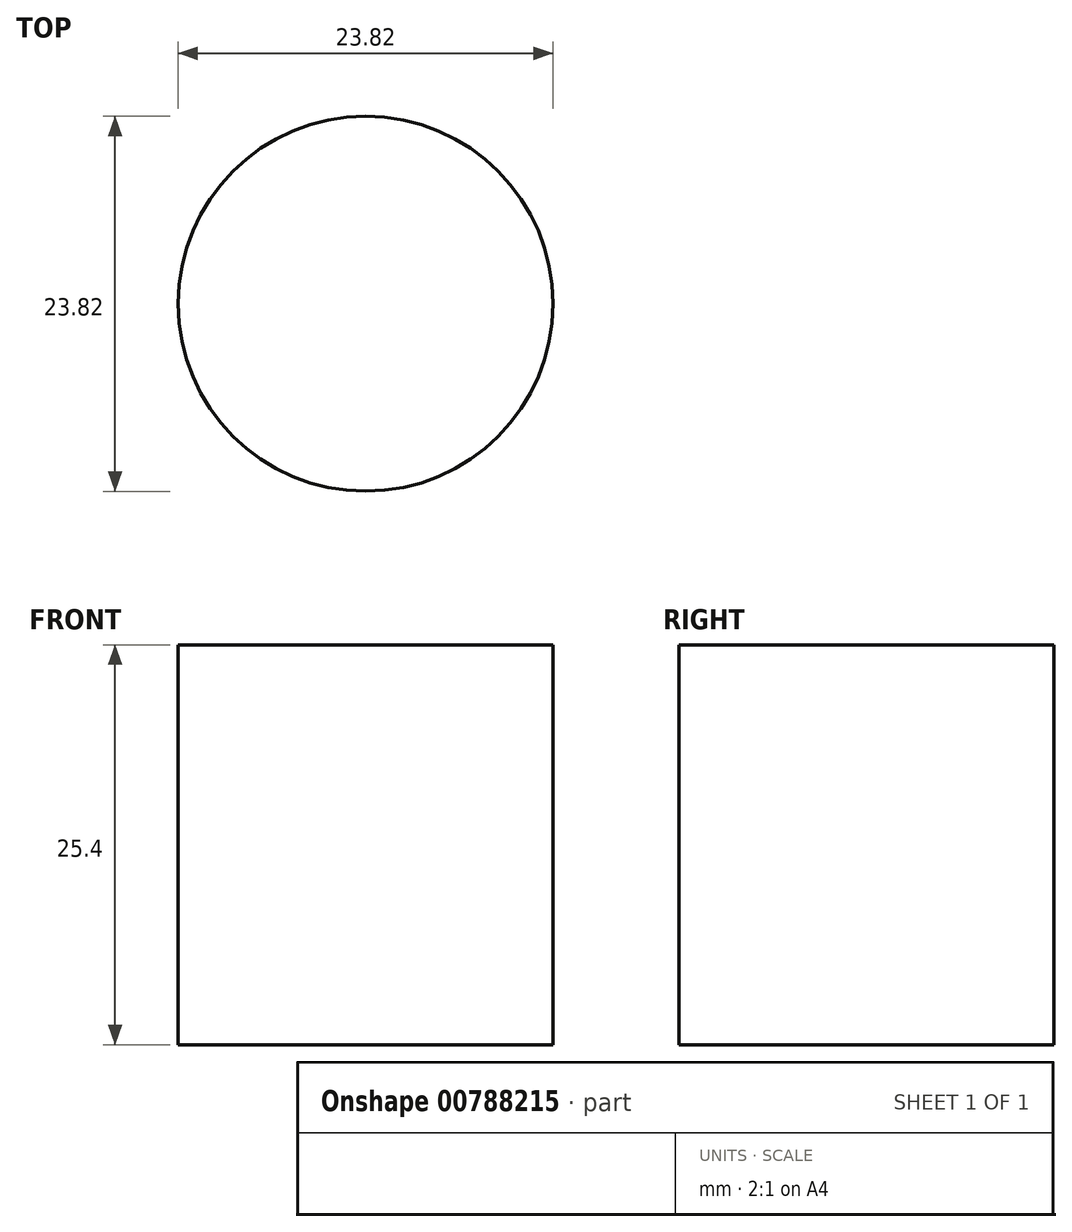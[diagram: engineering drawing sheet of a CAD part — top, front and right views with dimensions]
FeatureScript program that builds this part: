
annotation { "Feature Type Name" : "Feature", "Feature Type Description" : "" }
export const myFeature = defineFeature(function(context is Context, id is Id, definition is map)
    precondition{}
    {
        {
            var Q0;
            Q0=qCreatedBy(makeId("Top.planeOp"),FACE);
            var sketch = newSketch(context, id + "F0", { "sketchPlane" : qUnion([Q0])});
            skCircle(sketch, "E0", {"center": v(0, 0) * mm, "radius": 11.9 * mm});
            skSolve(sketch);
        }
        {
            var Q0;
            Q0 = qSketchRegion(id + "F0", true);
            extrude(context, id + "F1", {"entities" : qUnion([Q0]), "depth" : 25.4 * mm, "offsetDistance" : 25.4 * mm});
        }
    });
